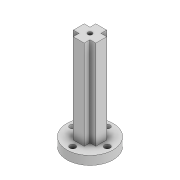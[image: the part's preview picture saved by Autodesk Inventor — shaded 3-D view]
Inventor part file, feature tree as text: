
AUTODESK INVENTOR PART (.ipt)
format: ipt  version: 2022 (Build 260153000, 153)  size: 127,488 bytes
history: native  units: mm
features: extrude x4, sketch x4, pattern_circular x1
ambient origin geometry x8: Origin, YZ Plane, XZ Plane, XY Plane, X Axis, Y Axis, Z Axis, Center Point
bodies: Solid1 (feature_tree)
feature tree (9):
  extrude  "Extrusion1"  Depth=3.0mm TaperAngle=0.0deg
  extrude  "Extrusion2"  Depth=2.0mm
  pattern_circular  "Circular Pattern1"  Count=4 Angle=360.0deg
  extrude  "Extrusion3"  Depth=7.8mm
  extrude  "Extrusion4"  Depth=31.0mm TaperAngle=0.0deg
  sketch  "Sketch1"  dims[d0=16.0mm d1=3.0mm d2=0.0mm]
  sketch  "Sketch2"  dims[d3=2.0mm d4=6.0mm]
  sketch  "Sketch3"  dims[d5=3.0mm d6=0.0mm d7=40.0mm d8=360.0deg]
  sketch  "Sketch4"  dims[d10=7.8mm d11=7.8mm d12=31.0mm d13=0.0mm d14=2.0mm d15=2.0mm d16=1.5mm d17=8.0mm d18=0.0mm]
